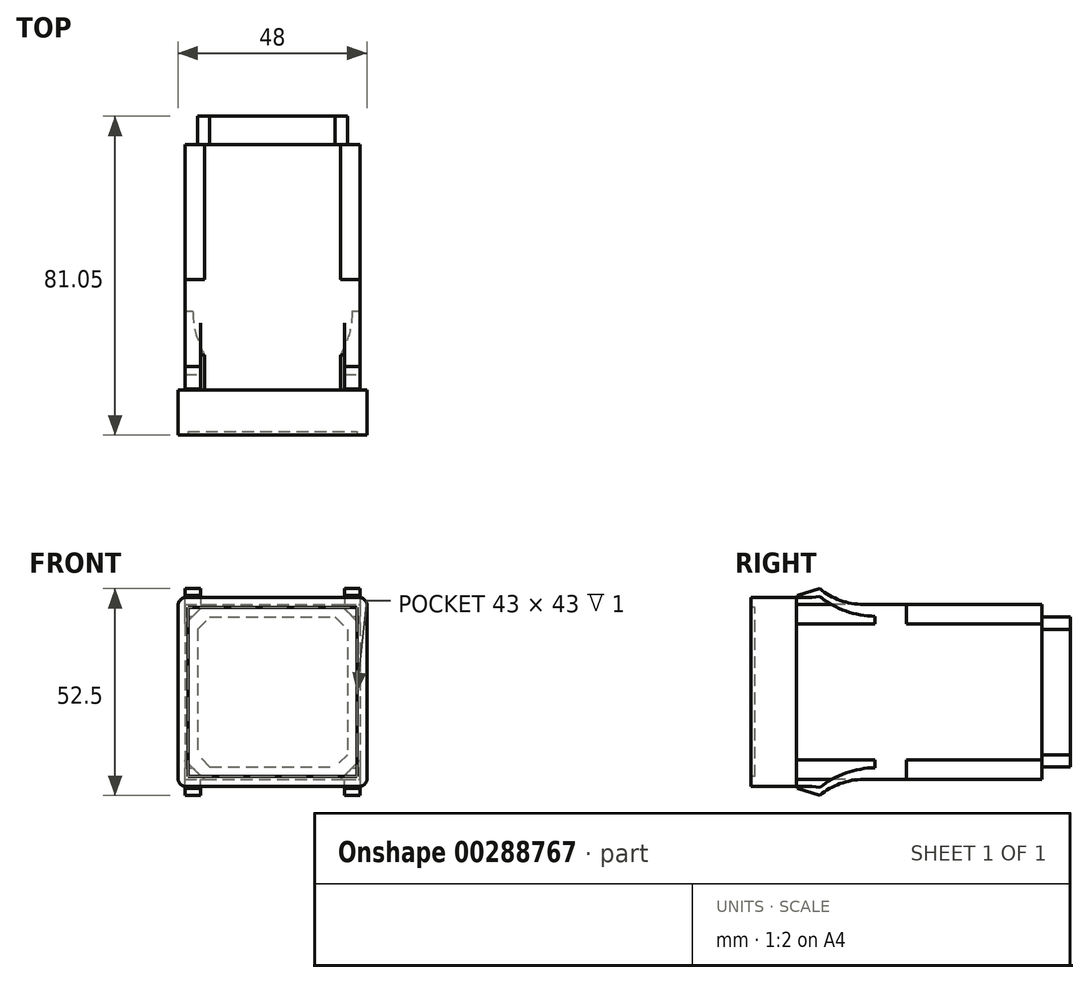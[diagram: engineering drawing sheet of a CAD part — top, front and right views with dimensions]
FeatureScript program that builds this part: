
annotation { "Feature Type Name" : "Feature", "Feature Type Description" : "" }
export const myFeature = defineFeature(function(context is Context, id is Id, definition is map)
    precondition{}
    {
        {
            var Q0;
            Q0=qCreatedBy(makeId("Front.planeOp"),FACE);
            var sketch = newSketch(context, id + "F0", { "sketchPlane" : qUnion([Q0])});
            skLineSegment(sketch, "E0.bottom", {"start": v(0, 0) * mm, "end": v(48, 0) * mm});
            skLineSegment(sketch, "E0.top", {"start": v(0, 48) * mm, "end": v(48, 48) * mm});
            skLineSegment(sketch, "E0.left", {"start": v(0, 0) * mm, "end": v(0, 48) * mm});
            skLineSegment(sketch, "E0.right", {"start": v(48, 0) * mm, "end": v(48, 48) * mm});
            skSolve(sketch);
        }
        {
            var Q0;
            Q0 = qSketchRegion(id + "F0", true);
            extrude(context, id + "F1", {"entities" : qUnion([Q0]), "depth" : 11.5 * mm});
        }
        {
            var Q0;
            Q0=makeQuery(id+"F1.opExtrude","CAP_FACE",FACE,{"disambiguationData":[OSD([sQuery(id+"F0.wireOp",EDGE,"E0.bottom"),sQuery(id+"F0.wireOp",EDGE,"E0.top"),sQuery(id+"F0.wireOp",EDGE,"E0.left"),sQuery(id+"F0.wireOp",EDGE,"E0.right")])],"isStart":false});
            var sketch = newSketch(context, id + "F2", { "sketchPlane" : qUnion([Q0])});
            skLineSegment(sketch, "E1.0", {"start": v(0, 48) * mm, "end": v(48, 48) * mm});
            skLineSegment(sketch, "E1.1", {"start": v(48, 0) * mm, "end": v(48, 48) * mm});
            skLineSegment(sketch, "E1.2", {"start": v(0, 0) * mm, "end": v(48, 0) * mm});
            skLineSegment(sketch, "E1.3", {"start": v(0, 0) * mm, "end": v(0, 48) * mm});
            skPoint(sketch, "E1.4", {"position": v(0, 24) * mm});
            skLineSegment(sketch, "E2.0", {"start": v(2.5, 45.5) * mm, "end": v(45.5, 45.5) * mm});
            skLineSegment(sketch, "E2.1", {"start": v(2.5, 2.5) * mm, "end": v(2.5, 45.5) * mm});
            skLineSegment(sketch, "E2.2", {"start": v(2.5, 2.5) * mm, "end": v(45.5, 2.5) * mm});
            skLineSegment(sketch, "E2.3", {"start": v(45.5, 2.5) * mm, "end": v(45.5, 45.5) * mm});
            skSolve(sketch);
        }
        {
            var Q0;
            Q0=makeQuery(id+"F2.imprint","IMPRINT",FACE,{"disambiguationData":[TD([[makeQuery(id+"F2.imprint","IMPRINT",EDGE,{"derivedFrom":sQuery(id+"F2.wireOp",EDGE,"E2.0")}),-1.0]])]});
            extrude(context, id + "F3", {"entities" : qUnion([Q0]), "operationType" : NewBodyOperationType.REMOVE, "oppositeDirection" : true, "depth" : 1 * mm});
        }
        {
            var Q0;
            Q0=makeQuery(id+"F1.opExtrude","SWEPT_EDGE",EDGE,{"disambiguationData":[OSD([sQuery(id+"F0.wireOp",EDGE,"E0.top"),sQuery(id+"F0.wireOp",EDGE,"E0.left")])]});
            var Q1;
            Q1=makeQuery(id+"F1.opExtrude","SWEPT_EDGE",EDGE,{"disambiguationData":[OSD([sQuery(id+"F0.wireOp",EDGE,"E0.top"),sQuery(id+"F0.wireOp",EDGE,"E0.right")])]});
            var Q2;
            Q2=makeQuery(id+"F1.opExtrude","SWEPT_EDGE",EDGE,{"disambiguationData":[OSD([sQuery(id+"F0.wireOp",EDGE,"E0.bottom"),sQuery(id+"F0.wireOp",EDGE,"E0.right")])]});
            var Q3;
            Q3=makeQuery(id+"F1.opExtrude","SWEPT_EDGE",EDGE,{"disambiguationData":[OSD([sQuery(id+"F0.wireOp",EDGE,"E0.bottom"),sQuery(id+"F0.wireOp",EDGE,"E0.left")])]});
            fillet(context, id + "F4", {"entities" : qUnion([Q0, Q1, Q2, Q3]), "radius" : 2 * mm, "tangentPropagation" : true, "allowEdgeOverflow" : false});
        }
        {
            var Q0;
            Q0=makeQuery(id+"F1.opExtrude","CAP_FACE",FACE,{"disambiguationData":[OSD([sQuery(id+"F0.wireOp",EDGE,"E0.bottom"),sQuery(id+"F0.wireOp",EDGE,"E0.top"),sQuery(id+"F0.wireOp",EDGE,"E0.left"),sQuery(id+"F0.wireOp",EDGE,"E0.right")])],"isStart":true});
            var sketch = newSketch(context, id + "F5", { "sketchPlane" : qUnion([Q0])});
            skLineSegment(sketch, "E3", {"start": v(-24, 48) * mm, "end": v(-24, 0) * mm, "construction": true});
            skLineSegment(sketch, "E4.bottom", {"start": v(-1.75, 46.25) * mm, "end": v(-46.25, 46.25) * mm});
            skLineSegment(sketch, "E4.top", {"start": v(-1.75, 1.75) * mm, "end": v(-46.25, 1.75) * mm});
            skLineSegment(sketch, "E4.left", {"start": v(-1.75, 46.25) * mm, "end": v(-1.75, 1.75) * mm});
            skLineSegment(sketch, "E4.right", {"start": v(-46.25, 46.25) * mm, "end": v(-46.25, 1.75) * mm});
            skPoint(sketch, "E4.middle", {"position": v(-24, 24) * mm});
            skSolve(sketch);
        }
        {
            var Q0;
            Q0 = qSketchRegion(id + "F5", true);
            extrude(context, id + "F6", {"entities" : qUnion([Q0]), "operationType" : NewBodyOperationType.ADD, "depth" : 62.4 * mm});
        }
        {
            var Q0;
            Q0=makeQuery(id+"F6.opExtrude","SWEPT_EDGE",EDGE,{"disambiguationData":[OSD([sQuery(id+"F5.wireOp",EDGE,"E4.bottom"),sQuery(id+"F5.wireOp",EDGE,"E4.right")])]});
            var Q1;
            Q1=makeQuery(id+"F6.opExtrude","SWEPT_EDGE",EDGE,{"disambiguationData":[OSD([sQuery(id+"F5.wireOp",EDGE,"E4.bottom"),sQuery(id+"F5.wireOp",EDGE,"E4.left")])]});
            var Q2;
            Q2=makeQuery(id+"F6.opExtrude","SWEPT_EDGE",EDGE,{"disambiguationData":[OSD([sQuery(id+"F5.wireOp",EDGE,"E4.top"),sQuery(id+"F5.wireOp",EDGE,"E4.right")])]});
            var Q3;
            Q3=makeQuery(id+"F6.opExtrude","SWEPT_EDGE",EDGE,{"disambiguationData":[OSD([sQuery(id+"F5.wireOp",EDGE,"E4.top"),sQuery(id+"F5.wireOp",EDGE,"E4.left")])]});
            chamfer(context, id + "F7", {"entities" : qUnion([Q0, Q1, Q2, Q3]), "width" : 5 * mm, "tangentPropagation" : true});
        }
        {
            var Q0;
            Q0=makeQuery(id+"F6.opExtrude","CAP_FACE",FACE,{"disambiguationData":[OSD([sQuery(id+"F5.wireOp",EDGE,"E4.bottom"),sQuery(id+"F5.wireOp",EDGE,"E4.top"),sQuery(id+"F5.wireOp",EDGE,"E4.left"),sQuery(id+"F5.wireOp",EDGE,"E4.right")])],"isStart":false});
            var sketch = newSketch(context, id + "F8", { "sketchPlane" : qUnion([Q0])});
            skLineSegment(sketch, "E5.0", {"start": v(-6.75, 46.25) * mm, "end": v(-41.25, 46.25) * mm, "construction": true});
            skLineSegment(sketch, "E5.1", {"start": v(-1.75, 41.25) * mm, "end": v(-6.75, 46.25) * mm, "construction": true});
            skLineSegment(sketch, "E5.2", {"start": v(-1.75, 41.25) * mm, "end": v(-1.75, 6.75) * mm, "construction": true});
            skLineSegment(sketch, "E5.3", {"start": v(-6.75, 1.75) * mm, "end": v(-1.75, 6.75) * mm, "construction": true});
            skLineSegment(sketch, "E5.4", {"start": v(-6.75, 1.75) * mm, "end": v(-41.25, 1.75) * mm, "construction": true});
            skLineSegment(sketch, "E5.5", {"start": v(-46.25, 41.25) * mm, "end": v(-46.25, 6.75) * mm, "construction": true});
            skLineSegment(sketch, "E5.6", {"start": v(-46.25, 6.75) * mm, "end": v(-41.25, 1.75) * mm, "construction": true});
            skLineSegment(sketch, "E5.7", {"start": v(-41.25, 46.25) * mm, "end": v(-46.25, 41.25) * mm, "construction": true});
            skLineSegment(sketch, "E6.0", {"start": v(-4.95, 39.92) * mm, "end": v(-8.08, 43.05) * mm});
            skLineSegment(sketch, "E6.1", {"start": v(-4.95, 39.92) * mm, "end": v(-4.95, 8.08) * mm});
            skLineSegment(sketch, "E6.2", {"start": v(-8.08, 43.05) * mm, "end": v(-39.92, 43.05) * mm});
            skLineSegment(sketch, "E6.3", {"start": v(-8.08, 4.95) * mm, "end": v(-4.95, 8.08) * mm});
            skLineSegment(sketch, "E6.4", {"start": v(-39.92, 43.05) * mm, "end": v(-43.05, 39.92) * mm});
            skLineSegment(sketch, "E6.5", {"start": v(-43.05, 39.92) * mm, "end": v(-43.05, 8.08) * mm});
            skLineSegment(sketch, "E6.6", {"start": v(-43.05, 8.08) * mm, "end": v(-39.92, 4.95) * mm});
            skLineSegment(sketch, "E6.7", {"start": v(-8.08, 4.95) * mm, "end": v(-39.92, 4.95) * mm});
            skLineSegment(sketch, "E7", {"start": v(-43.05, 24) * mm, "end": v(-4.95, 24) * mm, "construction": true});
            skSolve(sketch);
        }
        {
            var Q0;
            Q0=makeQuery(id+"F8.imprint","IMPRINT",FACE,{"disambiguationData":[TD([[makeQuery(id+"F8.imprint","IMPRINT",EDGE,{"derivedFrom":sQuery(id+"F8.wireOp",EDGE,"E6.0")}),1.0]])]});
            extrude(context, id + "F9", {"entities" : qUnion([Q0]), "operationType" : NewBodyOperationType.ADD, "depth" : 7.15 * mm});
        }
        {
            var Q0;
            Q0=makeQuery(id+"F6.opExtrude","SWEPT_FACE",FACE,{"disambiguationData":[OSD([sQuery(id+"F5.wireOp",EDGE,"E4.right")])]});
            var sketch = newSketch(context, id + "F10", { "sketchPlane" : qUnion([Q0])});
            skLineSegment(sketch, "E8", {"start": v(0, 41.25) * mm, "end": v(20, 41.25) * mm, "construction": true});
            skLineSegment(sketch, "E9", {"start": v(20, 41.25) * mm, "end": v(20, 43.25) * mm});
            skArc(sketch, "E10", {"start": v(5.94, 48.25) * mm, "mid": v(12.55, 44.57) * mm, "end": v(20, 43.25) * mm});
            skLineSegment(sketch, "E11", {"start": v(5.94, 48.25) * mm, "end": v(3.96, 48) * mm});
            skLineSegment(sketch, "E12", {"start": v(3.96, 48) * mm, "end": v(0.2, 48) * mm});
            skLineSegment(sketch, "E13", {"start": v(0.2, 48) * mm, "end": v(0.2, 48.5) * mm});
            skLineSegment(sketch, "E14", {"start": v(0.2, 48.5) * mm, "end": v(5.94, 50.25) * mm});
            skArc(sketch, "E15", {"start": v(5.94, 50.25) * mm, "mid": v(11.12, 47.28) * mm, "end": v(17, 46.25) * mm});
            skLineSegment(sketch, "E16", {"start": v(17, 46.25) * mm, "end": v(20, 46.25) * mm});
            skLineSegment(sketch, "E17", {"start": v(20, 46.25) * mm, "end": v(28, 46.25) * mm});
            skLineSegment(sketch, "E18", {"start": v(20, 41.25) * mm, "end": v(28, 41.25) * mm});
            skLineSegment(sketch, "E19", {"start": v(28, 46.25) * mm, "end": v(28, 41.25) * mm});
            skLineSegment(sketch, "E20", {"start": v(0, 24) * mm, "end": v(10.95, 24) * mm});
            skLineSegment(sketch, "E21.MirrorCS", {"start": v(0.2, 0) * mm, "end": v(0.2, -0.5) * mm});
            skLineSegment(sketch, "E22.MirrorCS", {"start": v(20, 1.75) * mm, "end": v(28, 1.75) * mm});
            skLineSegment(sketch, "E23.MirrorCS", {"start": v(17, 1.75) * mm, "end": v(20, 1.75) * mm});
            skArc(sketch, "E24.MirrorCS", {"start": v(5.94, -2.25) * mm, "mid": v(11.12, 0.72) * mm, "end": v(17, 1.75) * mm});
            skLineSegment(sketch, "E25.MirrorCS", {"start": v(0.2, -0.5) * mm, "end": v(5.94, -2.25) * mm});
            skLineSegment(sketch, "E26.MirrorCS", {"start": v(20, 6.75) * mm, "end": v(28, 6.75) * mm});
            skLineSegment(sketch, "E27.MirrorCS", {"start": v(3.96, 0) * mm, "end": v(0.2, 0) * mm});
            skLineSegment(sketch, "E28.MirrorCS", {"start": v(5.94, -0.25) * mm, "end": v(3.96, 0) * mm});
            skLineSegment(sketch, "E29.MirrorCS", {"start": v(20, 6.75) * mm, "end": v(20, 4.75) * mm});
            skLineSegment(sketch, "E30.MirrorCS", {"start": v(28, 1.75) * mm, "end": v(28, 6.75) * mm});
            skArc(sketch, "E31.MirrorCS", {"start": v(5.94, -0.25) * mm, "mid": v(12.55, 3.43) * mm, "end": v(20, 4.75) * mm});
            skSolve(sketch);
        }
        {
            var Q0;
            Q0 = qSketchRegion(id + "F10", true);
            var Q1;
            Q1=makeQuery(id+"F6.opExtrude","SWEPT_FACE",FACE,{"disambiguationData":[OSD([sQuery(id+"F5.wireOp",EDGE,"E4.left")])]});
            extrude(context, id + "F11", {"entities" : qUnion([Q0]), "operationType" : NewBodyOperationType.ADD, "endBound" : BoundingType.UP_TO_SURFACE, "oppositeDirection" : true, "endBoundEntityFace" : qUnion([Q1]), "depth" : 25 * mm});
        }
        {
            var Q0;
            Q0=makeQuery(id+"F11.boolean.opBoolean","MERGE",FACE,{"derivedFrom":[makeQuery(id+"F6.opExtrude","SWEPT_FACE",FACE,{"disambiguationData":[OSD([sQuery(id+"F5.wireOp",EDGE,"E4.bottom")])]}),makeQuery(id+"F11.opExtrude","SWEPT_FACE",FACE,{"disambiguationData":[OSD([sQuery(id+"F10.wireOp",EDGE,"E16"),sQuery(id+"F10.wireOp",EDGE,"E17")])]})]});
            var sketch = newSketch(context, id + "F12", { "sketchPlane" : qUnion([Q0])});
            skLineSegment(sketch, "E32.bottom", {"start": v(41.25, 28) * mm, "end": v(6.75, 28) * mm});
            skLineSegment(sketch, "E32.top", {"start": v(41.25, 0) * mm, "end": v(6.75, 0) * mm});
            skLineSegment(sketch, "E32.left", {"start": v(41.25, 28) * mm, "end": v(41.25, 17) * mm});
            skLineSegment(sketch, "E32.right", {"start": v(6.75, 28) * mm, "end": v(6.75, 17) * mm});
            skLineSegment(sketch, "E33.bottom", {"start": v(41.25, 17) * mm, "end": v(42.25, 17) * mm});
            skLineSegment(sketch, "E33.top", {"start": v(41.25, 0) * mm, "end": v(42.25, 0) * mm});
            skLineSegment(sketch, "E33.right", {"start": v(42.25, 17) * mm, "end": v(42.25, 0) * mm});
            skLineSegment(sketch, "E34", {"start": v(24, 28) * mm, "end": v(24, 21.37) * mm});
            skLineSegment(sketch, "E35.MirrorCS", {"start": v(6.75, 17) * mm, "end": v(5.75, 17) * mm});
            skLineSegment(sketch, "E36.MirrorCS", {"start": v(6.75, 0) * mm, "end": v(5.75, 0) * mm});
            skLineSegment(sketch, "E37.MirrorCS", {"start": v(5.75, 17) * mm, "end": v(5.75, 0) * mm});
            skSolve(sketch);
        }
        {
            var Q0;
            Q0 = qSketchRegion(id + "F12", true);
            var Q1;
            Q1=makeQuery(id+"F1.opExtrude","SWEPT_BODY",BODY,{"disambiguationData":[OSD([sQuery(id+"F0.wireOp",EDGE,"E0.bottom"),sQuery(id+"F0.wireOp",EDGE,"E0.top"),sQuery(id+"F0.wireOp",EDGE,"E0.left"),sQuery(id+"F0.wireOp",EDGE,"E0.right")])]});
            extrude(context, id + "F13", {"entities" : qUnion([Q0]), "operationType" : NewBodyOperationType.REMOVE, "depth" : 25 * mm});
        }
        {
            var Q0;
            Q0=makeQuery(id+"F11.boolean.opBoolean","MERGE",FACE,{"derivedFrom":[makeQuery(id+"F6.opExtrude","SWEPT_FACE",FACE,{"disambiguationData":[OSD([sQuery(id+"F5.wireOp",EDGE,"E4.top")])]}),makeQuery(id+"F11.opExtrude","SWEPT_FACE",FACE,{"disambiguationData":[OSD([sQuery(id+"F10.wireOp",EDGE,"E22.MirrorCS"),sQuery(id+"F10.wireOp",EDGE,"E23.MirrorCS")])]})]});
            var sketch = newSketch(context, id + "F14", { "sketchPlane" : qUnion([Q0])});
            skLineSegment(sketch, "E38.0", {"start": v(42.25, -17) * mm, "end": v(42.25, 0) * mm});
            skLineSegment(sketch, "E38.1", {"start": v(41.25, 0) * mm, "end": v(42.25, 0) * mm});
            skLineSegment(sketch, "E38.2", {"start": v(41.25, 0) * mm, "end": v(6.75, 0) * mm});
            skLineSegment(sketch, "E38.3", {"start": v(41.25, -17) * mm, "end": v(42.25, -17) * mm});
            skLineSegment(sketch, "E38.4", {"start": v(41.25, -28) * mm, "end": v(41.25, -17) * mm});
            skLineSegment(sketch, "E38.5", {"start": v(6.75, 0) * mm, "end": v(5.75, 0) * mm});
            skLineSegment(sketch, "E38.6", {"start": v(5.75, -17) * mm, "end": v(5.75, 0) * mm});
            skLineSegment(sketch, "E38.7", {"start": v(6.75, -17) * mm, "end": v(5.75, -17) * mm});
            skLineSegment(sketch, "E38.8", {"start": v(6.75, -28) * mm, "end": v(6.75, -17) * mm});
            skLineSegment(sketch, "E38.9", {"start": v(41.25, -28) * mm, "end": v(6.75, -28) * mm});
            skSolve(sketch);
        }
        {
            var Q0;
            Q0 = qSketchRegion(id + "F14", true);
            extrude(context, id + "F15", {"entities" : qUnion([Q0]), "operationType" : NewBodyOperationType.REMOVE, "depth" : 25 * mm});
        }
    });
